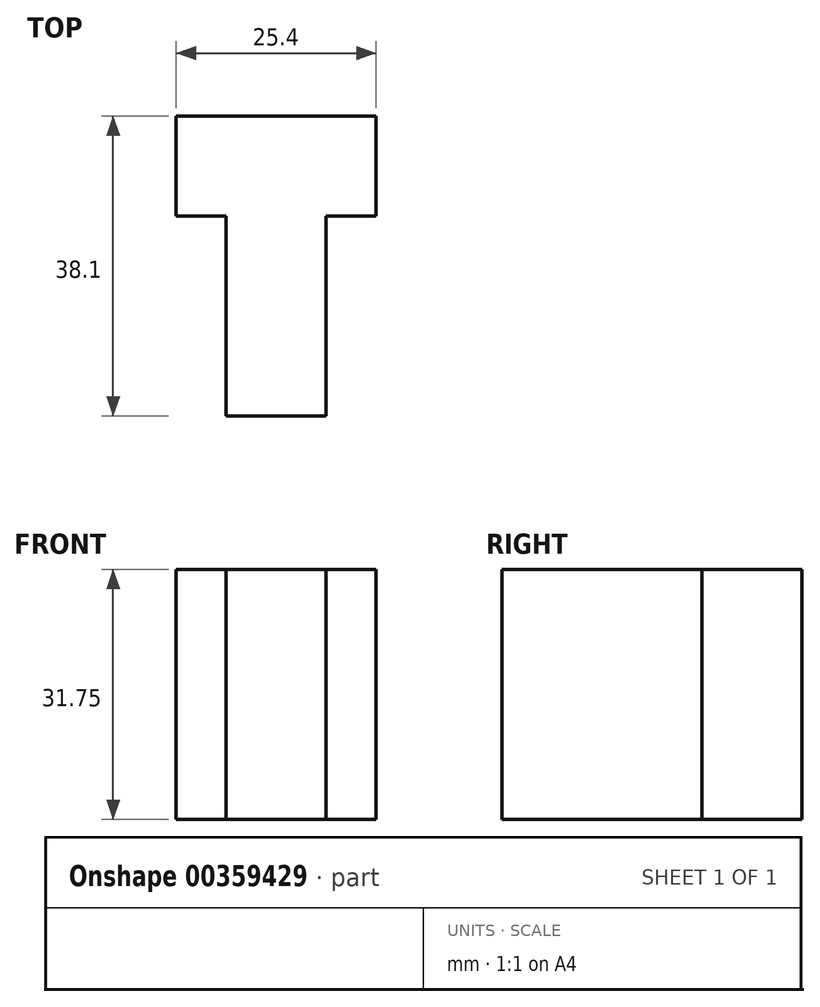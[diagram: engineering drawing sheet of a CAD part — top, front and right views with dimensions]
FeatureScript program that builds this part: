
annotation { "Feature Type Name" : "Feature", "Feature Type Description" : "" }
export const myFeature = defineFeature(function(context is Context, id is Id, definition is map)
    precondition{}
    {
        {
            var Q0;
            Q0=qCreatedBy(makeId("Top.planeOp"),FACE);
            var sketch = newSketch(context, id + "F0", { "sketchPlane" : qUnion([Q0])});
            skLineSegment(sketch, "E0", {"start": v(0, 4) * mm, "end": v(0, -8.7) * mm});
            skLineSegment(sketch, "E1", {"start": v(0, -8.7) * mm, "end": v(6.35, -8.7) * mm});
            skLineSegment(sketch, "E2", {"start": v(6.35, -34.1) * mm, "end": v(19.05, -34.1) * mm});
            skLineSegment(sketch, "E3", {"start": v(19.05, -34.1) * mm, "end": v(19.05, -8.7) * mm});
            skLineSegment(sketch, "E4", {"start": v(25.4, -8.7) * mm, "end": v(25.4, 4) * mm});
            skLineSegment(sketch, "E5", {"start": v(25.4, 4) * mm, "end": v(0, 4) * mm});
            skLineSegment(sketch, "E6", {"start": v(6.35, -34.1) * mm, "end": v(6.35, -8.7) * mm});
            skLineSegment(sketch, "E7", {"start": v(19.05, -8.7) * mm, "end": v(25.4, -8.7) * mm});
            skSolve(sketch);
        }
        {
            var Q0;
            Q0 = qSketchRegion(id + "F0", true);
            extrude(context, id + "F1", {"entities" : qUnion([Q0]), "depth" : 31.75 * mm});
        }
    });
